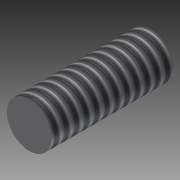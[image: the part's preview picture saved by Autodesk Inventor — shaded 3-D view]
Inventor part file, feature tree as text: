
AUTODESK INVENTOR PART (.ipt)
format: ipt  version: 2014 SP1 (Build 180222100, 222)  size: 87,040 bytes
history: native  units: in
note: dims shown in document units (in); Inventor stores cm internally (conversion verified against a paired STEP export)
features: extrude x1, thread x1, sketch x1
ambient origin geometry x8: Origin, YZ Plane, XZ Plane, XY Plane, X Axis, Y Axis, Z Axis, Center Point
bodies: Solid1 (feature_tree)
feature tree (3):
  extrude  "Extrusion1"  Depth=0.5in TaperAngle=0.0deg
  thread  "Thread1"  [1 undecoded]
  sketch  "Sketch1"  dims[d0=0.185in d1=0.5in d2=0.0in d3=1.0in d4=0.0in]
note: 1 required parameter value undecoded (feature->parameter linkage not recoverable at this tier; creation-order binding heuristic only, values carry confidence <= 0.55)
